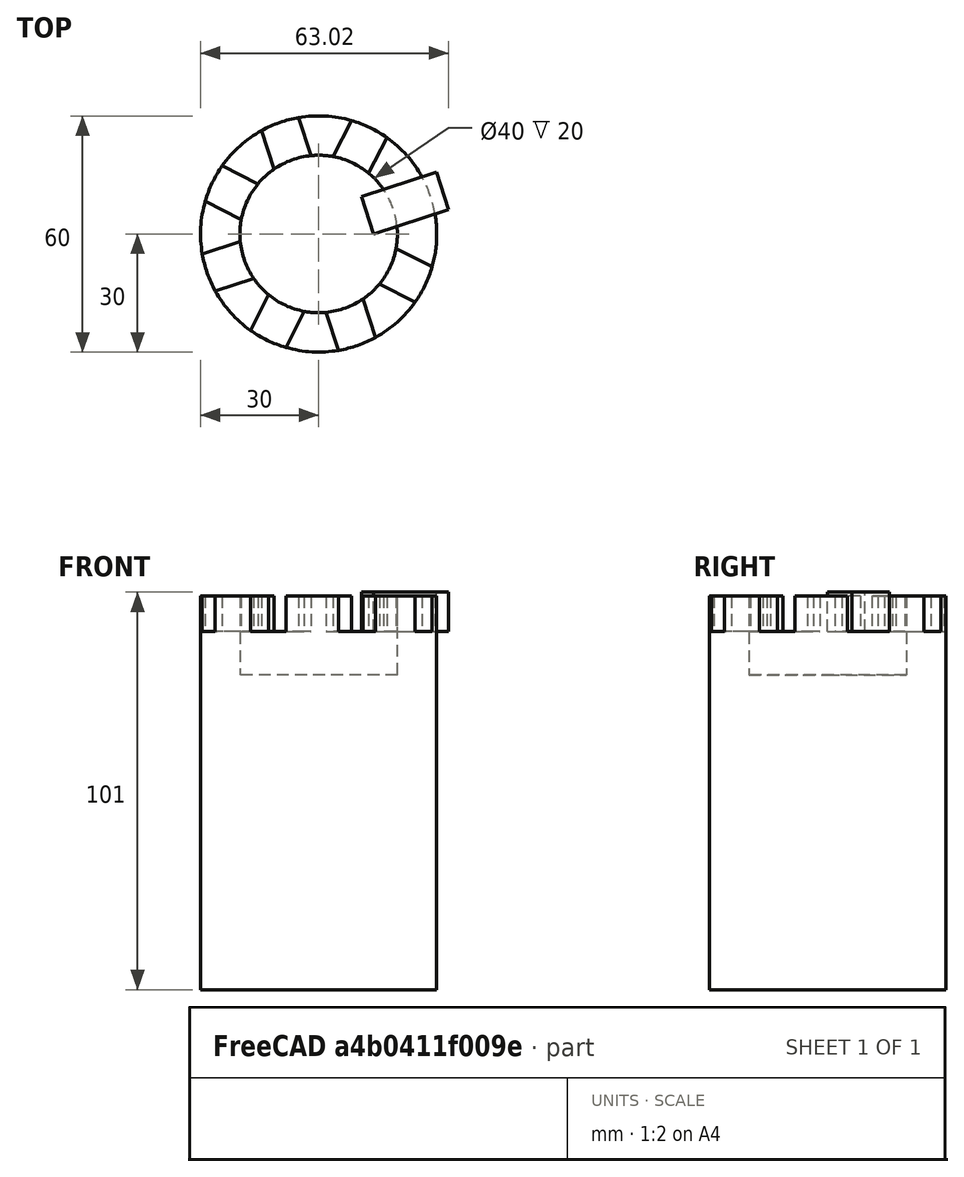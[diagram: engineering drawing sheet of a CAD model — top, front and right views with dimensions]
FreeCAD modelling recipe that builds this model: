
FCSTD DOCUMENT  (FreeCAD 0.21R33694 (Git))
Label: OJT1_T11R03_torre
License: All rights reserved
LicenseURL: https://en.wikipedia.org/wiki/All_rights_reserved
objects: Part::Cylinder×2, Part::Cut×2, Part::Box×1, Part::FeaturePython×1
note: 5 computed .brp shape members not serialized (recipe doc carries the construction recipe); baked Part::Feature solids carry a one-line shape summary decoded from their .brp

FEATURE [Part::Cylinder] Cylinder  label="Cilindre"
  Angle = 360
  AttacherType = Attacher::AttachEngine3D
  FirstAngle = 0
  Height = 100
  Radius = 30
  SecondAngle = 0
FEATURE [Part::Cylinder] Cylinder001  label="Cilindre001"
  Angle = 360
  AttacherType = Attacher::AttachEngine3D
  FirstAngle = 0
  Height = 20
  Placement = pos=(0,0,80) rot=(0,0,1;0rad)
  Radius = 20
  SecondAngle = 0
FEATURE [Part::Cut] Cut  label="Torre"
  Base = -> Cylinder
  Tool = -> Cylinder001
FEATURE [Part::Box] Box  label="Cub"
  AttacherType = Attacher::AttachEngine3D
  Height = 10
  Length = 20
  Placement = pos=(14,0,91) rot=(0,0,1;0.314159rad)
  Width = 10
FEATURE [Part::FeaturePython] Array  label="Rectangles"  # Draft array (typed FeaturePython)
  AlwaysSyncPlacement = false
  Angle = 360
  ArrayType = 1
  Axis = (0,0,1)
  Base = -> Box
  Center = (0,0,0)
  Count = 8
  ExpandArray = false
  Fuse = false
  IntervalAxis = (0,0,0)
  IntervalX = (100,0,0)
  IntervalY = (0,100,0)
  IntervalZ = (0,0,100)
  NumberCircles = 3
  NumberPolar = 8
  NumberX = 2
  NumberY = 2
  NumberZ = 1
  PlacementList = 8 placements: [(14,0,91),(9.89949,9.89949,91),(0,14,91),(-9.89949,9.89949,91),(-14,1.71451e-15,91),(-9.89949,-9.89949,91),(-3.10862e-15,-14,91),(9.89949,-9.89949,91)]
  RadialDistance = 50
  ScaleList = (8) [(1,1,1),(1,1,1),(1,1,1),(1,1,1),(1,1,1),(1,1,1),(1,1,1),(1,1,1)]
  Symmetry = 1
  TangentialDistance = 25
FEATURE [Part::Cut] Cut001  label="Castell"
  Base = -> Cut
  Tool = -> Array
